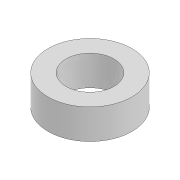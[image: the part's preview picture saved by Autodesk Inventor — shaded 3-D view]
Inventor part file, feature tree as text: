
AUTODESK INVENTOR PART (.ipt)
format: ipt  version: 2022 (Build 260153000, 153)  size: 81,920 bytes
history: native  units: mm
features: extrude x1, sketch x1
ambient origin geometry x8: Origin, YZ Plane, XZ Plane, XY Plane, X Axis, Y Axis, Z Axis, Center Point
bodies: Solid1 (feature_tree)
feature tree (2):
  extrude  "Extrusion1"  Depth=2.5mm
  sketch  "Sketch1"  dims[d0=4.0mm d1=7.0mm d2=2.5mm d3=0.0mm]
